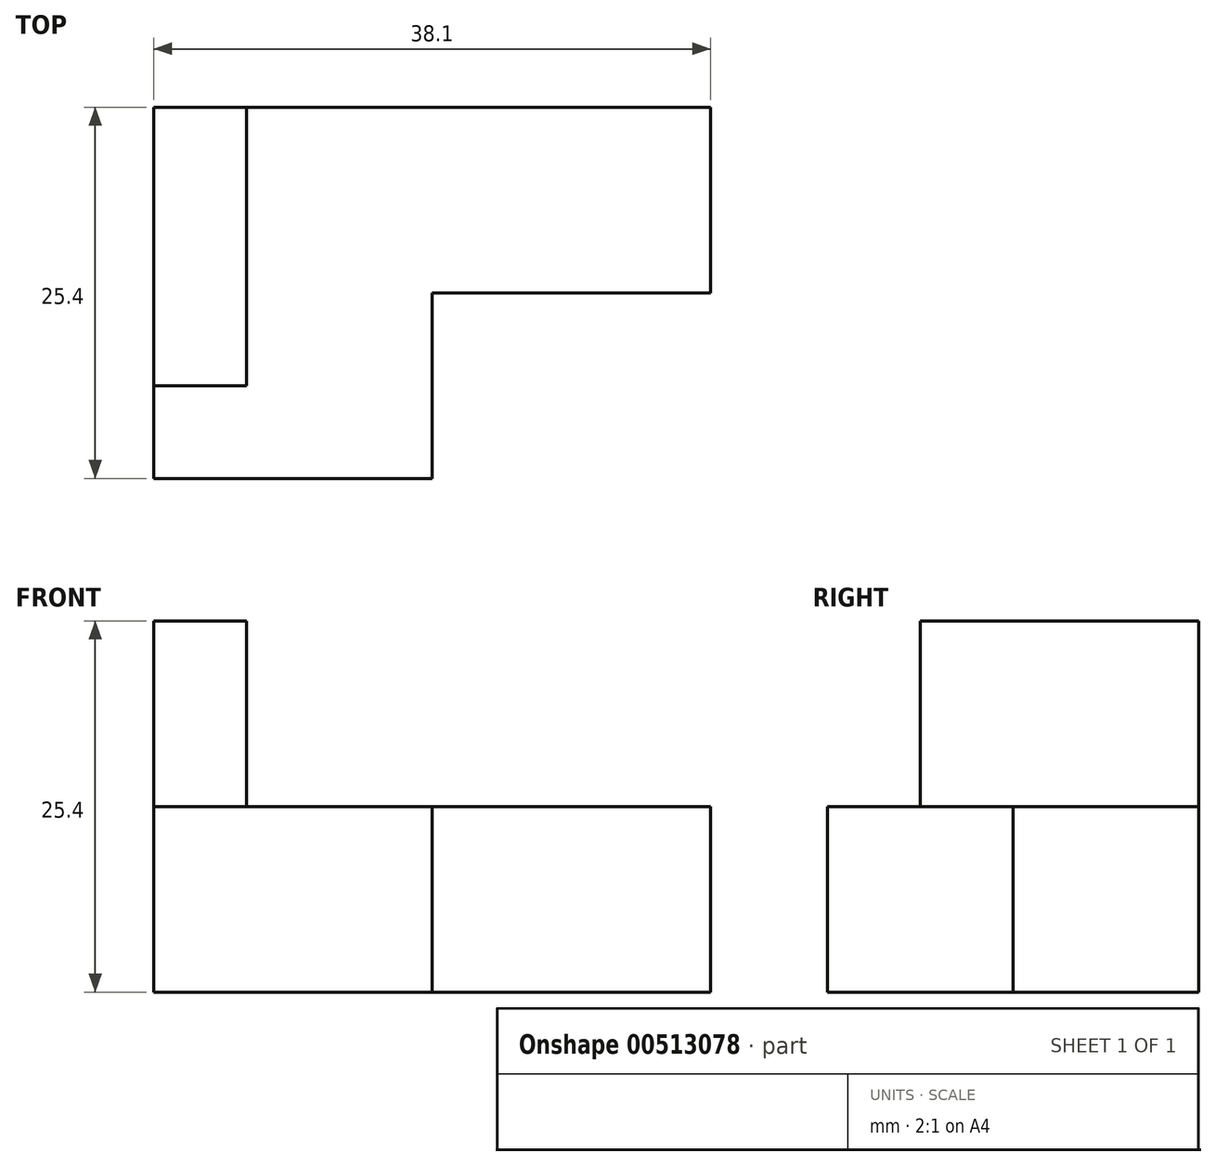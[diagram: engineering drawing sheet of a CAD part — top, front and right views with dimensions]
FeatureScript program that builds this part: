
annotation { "Feature Type Name" : "Feature", "Feature Type Description" : "" }
export const myFeature = defineFeature(function(context is Context, id is Id, definition is map)
    precondition{}
    {
        {
            var Q0;
            Q0=qCreatedBy(makeId("Top.planeOp"),FACE);
            var sketch = newSketch(context, id + "F0", { "sketchPlane" : qUnion([Q0])});
            skLineSegment(sketch, "E0", {"start": v(0, -25.4) * mm, "end": v(0, 0) * mm});
            skLineSegment(sketch, "E1", {"start": v(0, 0) * mm, "end": v(38.1, 0) * mm});
            skLineSegment(sketch, "E2", {"start": v(38.1, 0) * mm, "end": v(38.1, -12.7) * mm});
            skLineSegment(sketch, "E3", {"start": v(38.1, -12.7) * mm, "end": v(19.05, -12.7) * mm});
            skLineSegment(sketch, "E4", {"start": v(19.05, -12.7) * mm, "end": v(19.05, -25.4) * mm});
            skLineSegment(sketch, "E5", {"start": v(19.05, -25.4) * mm, "end": v(0, -25.4) * mm});
            skSolve(sketch);
        }
        {
            var Q0;
            Q0=qCreatedBy(makeId("Front.planeOp"),FACE);
            var sketch = newSketch(context, id + "F1", { "sketchPlane" : qUnion([Q0])});
            skLineSegment(sketch, "E6", {"start": v(0, 0) * mm, "end": v(0, 25.4) * mm});
            skLineSegment(sketch, "E7", {"start": v(0, 25.4) * mm, "end": v(6.35, 25.4) * mm});
            skLineSegment(sketch, "E8", {"start": v(6.35, 25.4) * mm, "end": v(6.35, 0) * mm});
            skLineSegment(sketch, "E9", {"start": v(6.35, 0) * mm, "end": v(0, 0) * mm});
            skSolve(sketch);
        }
        {
            var Q0;
            Q0=makeQuery(id+"F0.imprint","IMPRINT",FACE,{"disambiguationData":[TD([[makeQuery(id+"F0.imprint","IMPRINT",EDGE,{"derivedFrom":sQuery(id+"F0.wireOp",EDGE,"E0")}),-1.0]])]});
            extrude(context, id + "F2", {"entities" : qUnion([Q0]), "depth" : 12.7 * mm});
        }
        {
            var Q0;
            Q0=qSketchRegion(id+"F1",true);
            extrude(context, id + "F3", {"entities" : qUnion([Q0]), "operationType" : NewBodyOperationType.ADD, "depth" : 19.05 * mm});
        }
    });
